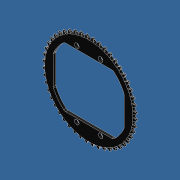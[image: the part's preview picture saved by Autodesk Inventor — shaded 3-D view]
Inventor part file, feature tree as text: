
AUTODESK INVENTOR PART (.ipt)
format: ipt  version: unknown  size: 2,009,600 bytes
history: native  units: in
note: dims shown in document units (in); Inventor stores cm internally (conversion verified against a paired STEP export)
features: sketch x3, extrude x2, boolean_combine x1, imported_body x1, hole x1, fillet x1
ambient origin geometry x8: Origin, YZ Plane, XZ Plane, XY Plane, X Axis, Y Axis, Z Axis, Center Point
feature tree (9):
  boolean_combine  "Combine1"
  imported_body  "Base1"
  extrude  "Extrusion1"  Depth=1.4875in
  extrude  "Extrusion2"  Depth=0.625in
  hole  "Hole1"  [1 undecoded]
  fillet  "Fillet1"  Radius=1.25in
  sketch  "Sketch1"  dims[d0=1.4875in d1=1.4875in]
  sketch  "Sketch2"  dims[d2=4.8695in d3=0.625in]
  sketch  "Sketch3"  dims[d4=0.625in d5=1.0in d6=0.0in d7=1.25in d8=1.25in d9=1.0in d10=0.0in d11=0.5in d12=0.5in d13=0.5in d14=0.5in d15=0.1406in d16=0.1406in d17=0.1406in d18=0.1406in d19=0.196in d20=0.75in d21=0.375in d22=0.25in d23=0.5635in d24=1.0in d25=0.8108in d26=0.125in]
note: 1 required parameter value undecoded (feature->parameter linkage not recoverable at this tier; creation-order binding heuristic only, values carry confidence <= 0.55)
